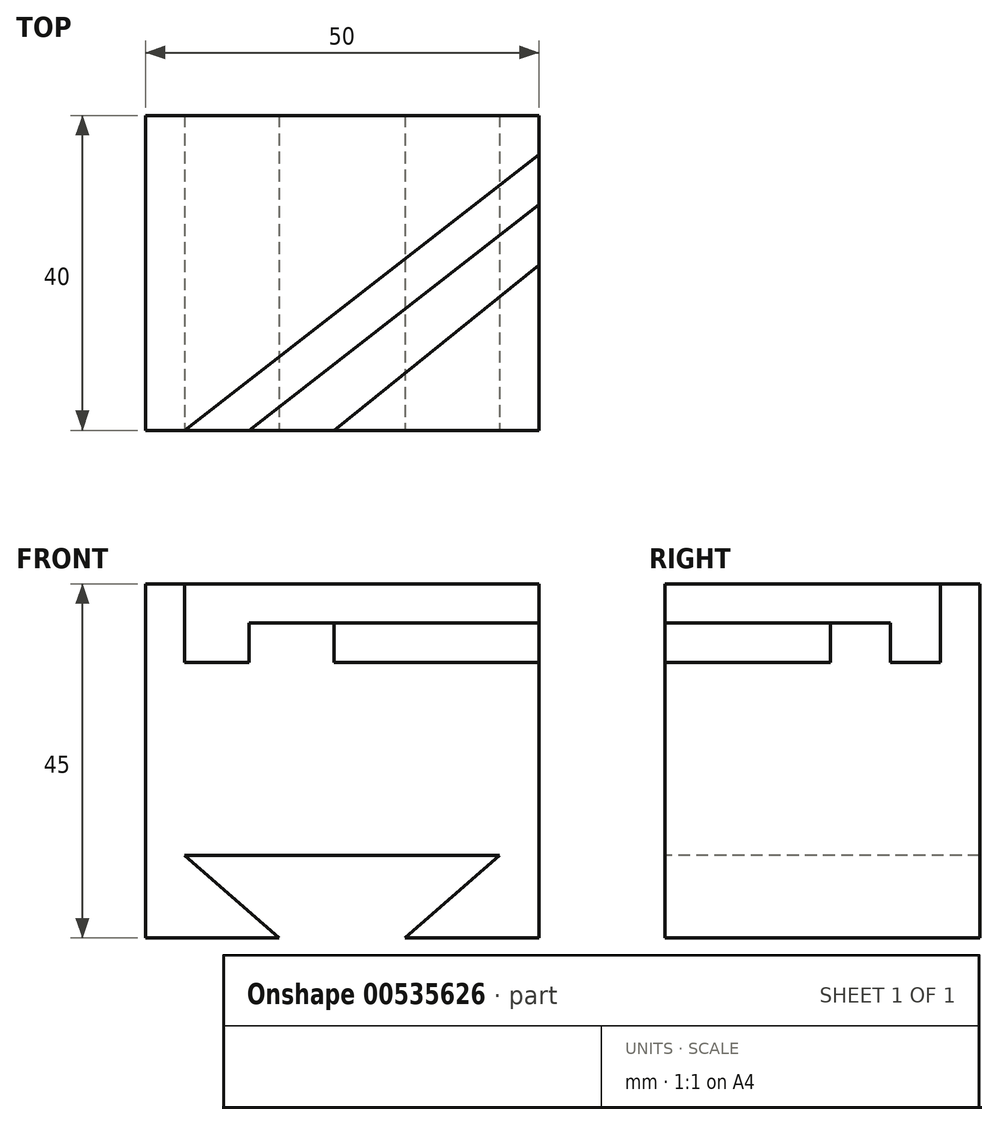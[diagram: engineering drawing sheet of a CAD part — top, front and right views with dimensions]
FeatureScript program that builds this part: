
annotation { "Feature Type Name" : "Feature", "Feature Type Description" : "" }
export const myFeature = defineFeature(function(context is Context, id is Id, definition is map)
    precondition{}
    {
        {
            var Q0;
            Q0=qCreatedBy(makeId("Front.planeOp"),FACE);
            var sketch = newSketch(context, id + "F0", { "sketchPlane" : qUnion([Q0])});
            skLineSegment(sketch, "E0.bottom", {"start": v(25, -20) * mm, "end": v(-25, -20) * mm});
            skLineSegment(sketch, "E0.top", {"start": v(25, 20) * mm, "end": v(-25, 20) * mm});
            skLineSegment(sketch, "E0.left", {"start": v(25, -20) * mm, "end": v(25, 20) * mm});
            skLineSegment(sketch, "E0.right", {"start": v(-25, -20) * mm, "end": v(-25, 20) * mm});
            skPoint(sketch, "E0.middle", {"position": v(0, 0) * mm});
            skSolve(sketch);
        }
        {
            var Q0;
            Q0=makeQuery(id+"F0.imprint","IMPRINT",FACE,{"disambiguationData":[TD([[makeQuery(id+"F0.imprint","IMPRINT",EDGE,{"derivedFrom":sQuery(id+"F0.wireOp",EDGE,"E0.bottom")}),-1.0]])]});
            extrude(context, id + "F1", {"entities" : qUnion([Q0]), "depth" : 40 * mm, "offsetDistance" : 25 * mm});
        }
        {
            var Q0;
            Q0=makeQuery(id+"F1.opExtrude","CAP_FACE",FACE,{"disambiguationData":[OSD([sQuery(id+"F0.wireOp",EDGE,"E0.bottom"),sQuery(id+"F0.wireOp",EDGE,"E0.top"),sQuery(id+"F0.wireOp",EDGE,"E0.left"),sQuery(id+"F0.wireOp",EDGE,"E0.right")])],"isStart":false});
            var sketch = newSketch(context, id + "F2", { "sketchPlane" : qUnion([Q0])});
            skLineSegment(sketch, "E1", {"start": v(-25, -20) * mm, "end": v(-8, -20) * mm});
            skLineSegment(sketch, "E2", {"start": v(-8, -20) * mm, "end": v(8, -20) * mm});
            skLineSegment(sketch, "E3", {"start": v(-8, -20) * mm, "end": v(-20, -9.52) * mm});
            skLineSegment(sketch, "E4", {"start": v(-20, -9.52) * mm, "end": v(0, -9.52) * mm});
            skLineSegment(sketch, "E5.MirrorCS", {"start": v(8, -20) * mm, "end": v(20, -9.52) * mm});
            skLineSegment(sketch, "E6.MirrorCS", {"start": v(20, -9.52) * mm, "end": v(0, -9.52) * mm});
            skSolve(sketch);
        }
        {
            var Q0;
            Q0=makeQuery(id+"F2.imprint","IMPRINT",FACE,{"disambiguationData":[TD([[makeQuery(id+"F2.imprint","IMPRINT",EDGE,{"derivedFrom":sQuery(id+"F2.wireOp",EDGE,"E2")}),-1.0]])]});
            extrude(context, id + "F3", {"entities" : qUnion([Q0]), "operationType" : NewBodyOperationType.REMOVE, "endBound" : BoundingType.THROUGH_ALL, "oppositeDirection" : true, "depth" : 25 * mm, "offsetDistance" : 25 * mm});
        }
        {
            var Q0;
            Q0=makeQuery(id+"F1.opExtrude","SWEPT_FACE",FACE,{"disambiguationData":[OSD([sQuery(id+"F0.wireOp",EDGE,"E0.top")])]});
            var sketch = newSketch(context, id + "F4", { "sketchPlane" : qUnion([Q0])});
            skLineSegment(sketch, "E7", {"start": v(-25, -40) * mm, "end": v(-25, 0) * mm});
            skLineSegment(sketch, "E8", {"start": v(-25, 0) * mm, "end": v(25, 0) * mm});
            skLineSegment(sketch, "E9", {"start": v(25, 0) * mm, "end": v(25, -5) * mm});
            skLineSegment(sketch, "E10", {"start": v(25, -5) * mm, "end": v(-20, -40) * mm});
            skLineSegment(sketch, "E11", {"start": v(-20, -40) * mm, "end": v(-25, -40) * mm});
            skLineSegment(sketch, "E12", {"start": v(-11.86, -40) * mm, "end": v(25, -11.33) * mm});
            skLineSegment(sketch, "E13", {"start": v(-1, -40) * mm, "end": v(25, -19) * mm});
            skSolve(sketch);
        }
        {
            var Q0;
            Q0=makeQuery(id+"F4.imprint","IMPRINT",FACE,{"disambiguationData":[TD([[makeQuery(id+"F4.imprint","IMPRINT",EDGE,{"derivedFrom":sQuery(id+"F4.wireOp",EDGE,"E7")}),-1.0]])]});
            extrude(context, id + "F5", {"entities" : qUnion([Q0]), "operationType" : NewBodyOperationType.ADD, "depth" : 5 * mm, "offsetDistance" : 25 * mm});
        }
        {
            var Q0;
            {var subQ0=sQuery(id+"F4.wireOp",EDGE,"E10");Q0=makeQuery(id+"F4.imprint","IMPRINT",FACE,{"disambiguationData":[TD([[makeQuery(id+"F4.imprint","IMPRINT",EDGE,{"derivedFrom":subQ0}),1.0]])]});}
            extrude(context, id + "F6", {"entities" : qUnion([Q0]), "operationType" : NewBodyOperationType.REMOVE, "oppositeDirection" : true, "depth" : 5 * mm, "offsetDistance" : 25 * mm});
        }
        {
            var Q0;
            {var subQ0=sQuery(id+"F4.wireOp",EDGE,"E13");Q0=makeQuery(id+"F4.imprint","IMPRINT",FACE,{"disambiguationData":[TD([[makeQuery(id+"F4.imprint","IMPRINT",EDGE,{"derivedFrom":subQ0}),-1.0]])]});}
            extrude(context, id + "F7", {"entities" : qUnion([Q0]), "operationType" : NewBodyOperationType.REMOVE, "oppositeDirection" : true, "depth" : 5 * mm, "offsetDistance" : 25 * mm});
        }
    });
